# Revit family: Door_SectionalOverhead_RW_Alumatite-VerticalLift
name_source: partatom
category: Doors
units: mm (PartAtom-declared; Revit-internal decimal feet)

## family parameters
Always vertical = Yes
Classification Number = 23.30.10.17.37.14
Cut with Voids When Loaded = No
Host = Wall
Room Calculation Point = No
Shared = No

## types (1)
- ByType
    ADA Compliant = Yes
    Aluminum Material = Metal - Aluminum - Richards Wilcox - Anodized - Clear
    Analytic Construction = <None>
    Assembly Code = B2030410
    CE Compliant = No
    Construction Details = http://www.arcat.com
    Define Thermal Properties by = Schematic Type
    Description = Richards-Wilcox Overhead Door as Specified
    Door Glazing = Glazing - Richards Wilcox - Clear
    Expected Lifespan (Years) = 0
    Frame Thickness = 0' - 4 3/4"
    Function = Interior
    Green Building-LEED = http://www.arcat.com
    Hardware Finish = Metal - Steel - Richards Wilcox - Galvanized
    Height = 9' - 2"
    Installation-Fabrication = http://www.rwdoors.com
    Keynote = 08360
    Maintenance Schedule (Months) = 0
    Manufacturer = Richards-Wilcox Canada
    Manufacturer Fax = 905-625-0057
    Manufacturer Website = http://www.rwdoors.com
    Model = As Specified
    Panel Height = 1' - 10"
    Panel Material - Exterior = Metal - Steel - Richards Wilcox - Painted - Silver - Multi-Rib
    Panel Material - Interior = Metal - Steel - Richards Wilcox - Painted - Silver - Ribbed
    Panel Width = 15' - 2"
    Panels = 5
    Product Data = http://www.arcat.com
    RO Offset = 0' - 0"
    R_Value = 0
    Revision = R1_12-2011
    Rough Height = 9' - 2"
    Rough Width = 15' - 0"
    Sales Information = http://www.rwdoors.com
    Send Message = http://www.arcat.com
    Shaft Diameter = 0' - 1"
    Sound Transmission Class (STC) = 0
    SpecWizard = http://www.arcat.com
    Specification = http://www.arcat.com
    Spring Length = 3' - 0"
    Spring Width = 16' - 0"
    Thickness = 0' - 1 1/2"
    URL = http://www.rwdoors.com
    Wall Closure = By host
    Warranty Duration (Years) = 0
    Width = 15' - 0"

## geometry (parser evidence)
native form markers: Blend x16, Sweep x21
no freeform markers — native parametric forms only
